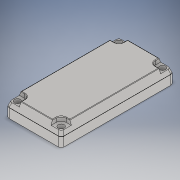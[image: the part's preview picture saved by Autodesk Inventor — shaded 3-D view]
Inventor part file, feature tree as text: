
AUTODESK INVENTOR PART (.ipt)
format: ipt  version: 2021.2 (Build 252289000, 289)  size: 261,632 bytes
history: native  units: mm
features: other x4, mirror x4, chamfer x4, extrude x3, fillet x2, sketch x2
ambient origin geometry x8: Origin, YZ Plane, XZ Plane, XY Plane, X Axis, Y Axis, Z Axis, Center Point
bodies: Body1 (feature_tree)
feature tree (19):
  other  "Sólido1"
  extrude  "Extrusión1"  Depth=40.6mm
  extrude  "Extrusión2"  Depth=0.2mm
  mirror  "Simetría1"
  mirror  "Simetría2"
  extrude  "Extrusión3"  Depth=0.2mm TaperAngle=0.0deg
  mirror  "Simetría3"
  mirror  "Simetría4"
  chamfer  "Chaflán1"  Distance=2.2mm
  chamfer  "Chaflán2"  Distance=2.2mm
  chamfer  "Chaflán3"  Distance=2.2mm
  chamfer  "Chaflán4"  Distance=1.5mm
  fillet  "Empalme1"  Radius=2.0mm
  fillet  "Empalme2"  Radius=2.0mm
  sketch  "Boceto1"  dims[d0=19.8mm d1=40.6mm]
  other  "Eje de trabajo1"
  other  "Eje de trabajo2"
  other  "Eje de trabajo3"
  sketch  "Boceto4"  dims[d2=6.4mm d3=0.0mm d6=3.6mm d8=1.5mm d9=0.0mm d10=2.2mm d11=2.2mm d12=2.2mm d13=1.5mm d14=0.0mm d15=3.0mm d16=2.0mm d17=3.490659mm d18=3.0mm d19=2.0mm d20=3.490659mm d21=3.0mm d22=2.0mm d23=3.490659mm d24=3.0mm d25=2.0mm d26=3.490659mm d27=1.0mm d28=0.2mm]
